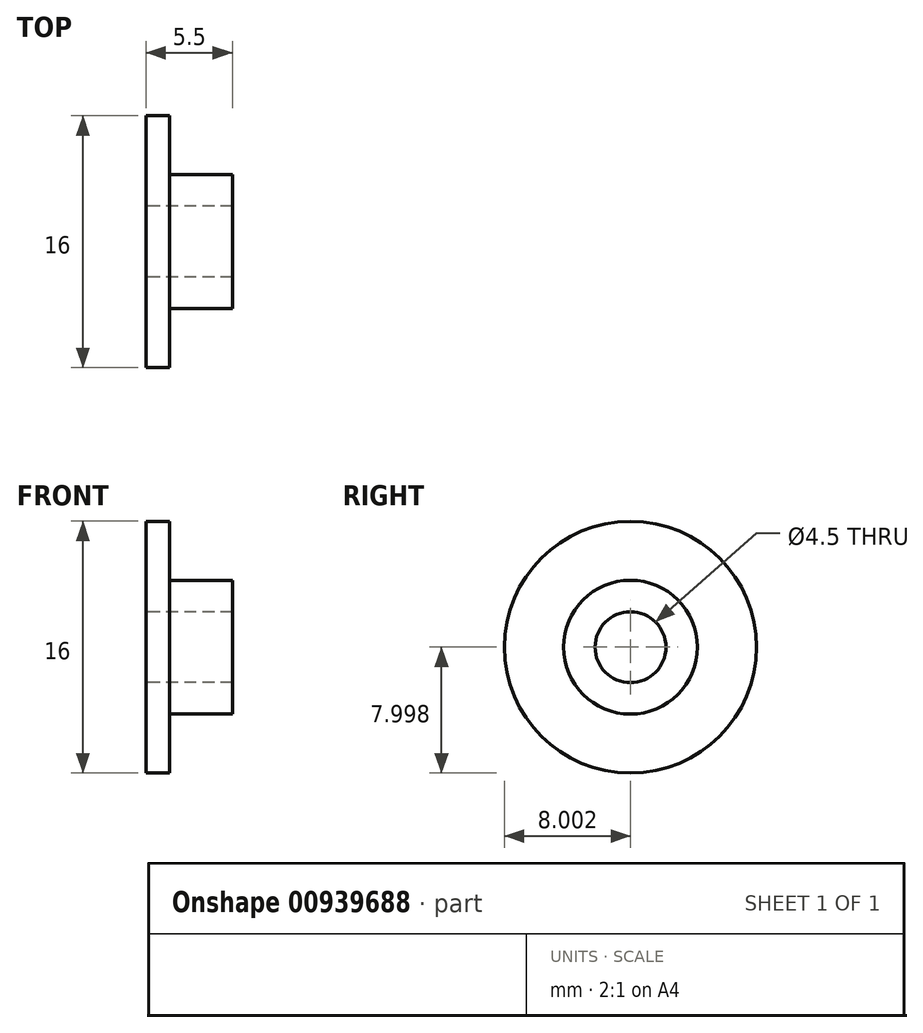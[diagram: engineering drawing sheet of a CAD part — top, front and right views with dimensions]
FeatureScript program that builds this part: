
annotation { "Feature Type Name" : "Feature", "Feature Type Description" : "" }
export const myFeature = defineFeature(function(context is Context, id is Id, definition is map)
    precondition{}
    {
        {
            var Q0;
            Q0=qCreatedBy(makeId("Right.planeOp"),FACE);
            var sketch = newSketch(context, id + "F0", { "sketchPlane" : qUnion([Q0])});
            skArc(sketch, "E0.0", {"start": v(7.2, 6.47) * mm, "mid": v(-5.3, 18.98) * mm, "end": v(-17.8, 6.47) * mm});
            skArc(sketch, "E1.0", {"start": v(9.7, 6.27) * mm, "mid": v(-5.3, 21.27) * mm, "end": v(-20.3, 6.27) * mm});
            skLineSegment(sketch, "E2.0.0", {"start": v(-20.3, -8.73) * mm, "end": v(9.7, -8.73) * mm});
            skLineSegment(sketch, "E2.0.1", {"start": v(9.7, -8.73) * mm, "end": v(9.7, -3.73) * mm});
            skLineSegment(sketch, "E2.0.2", {"start": v(9.7, -3.73) * mm, "end": v(9.7, 6.27) * mm});
            skLineSegment(sketch, "E2.0.4", {"start": v(-20.3, 6.27) * mm, "end": v(-20.3, -8.73) * mm});
            skLineSegment(sketch, "E3.0", {"start": v(-17.8, 6.47) * mm, "end": v(-17.8, -6.73) * mm});
            skLineSegment(sketch, "E4.0", {"start": v(-17.8, -6.73) * mm, "end": v(7.2, -6.73) * mm});
            skLineSegment(sketch, "E5.0", {"start": v(7.2, 6.47) * mm, "end": v(7.2, -6.73) * mm});
            skLineSegment(sketch, "E6.0.0", {"start": v(9.7, -8.73) * mm, "end": v(79.7, -8.73) * mm});
            skLineSegment(sketch, "E6.0.1", {"start": v(79.7, -8.73) * mm, "end": v(74.7, -3.73) * mm});
            skLineSegment(sketch, "E6.0.2", {"start": v(74.7, -3.73) * mm, "end": v(9.7, -3.73) * mm});
            skLineSegment(sketch, "E6.0.3", {"start": v(9.7, -3.73) * mm, "end": v(9.7, -8.73) * mm});
            skCircle(sketch, "E7", {"center": v(-5.3, 6.47) * mm, "radius": 12.5 * mm});
            skCircle(sketch, "E8", {"center": v(-5.3, 6.27) * mm, "radius": 5 * mm});
            skLineSegment(sketch, "E9", {"start": v(-17.8, 6.47) * mm, "end": v(-16.3, 6.47) * mm});
            skLineSegment(sketch, "E10", {"start": v(7.2, 6.47) * mm, "end": v(5.7, 6.47) * mm});
            skArc(sketch, "E11", {"start": v(5.7, 6.47) * mm, "mid": v(-5.3, 17.5) * mm, "end": v(-16.3, 6.47) * mm});
            skLineSegment(sketch, "E12", {"start": v(7.2, 6.47) * mm, "end": v(6.8, 6.47) * mm});
            skLineSegment(sketch, "E13", {"start": v(-17.8, 6.47) * mm, "end": v(-17.4, 6.47) * mm});
            skArc(sketch, "E14", {"start": v(6.8, 6.47) * mm, "mid": v(-5.3, 18.58) * mm, "end": v(-17.4, 6.47) * mm});
            skLineSegment(sketch, "E15", {"start": v(-17.4, 6.47) * mm, "end": v(-17.4, -6.73) * mm});
            skLineSegment(sketch, "E16", {"start": v(-16.3, 6.47) * mm, "end": v(-16.28, -6.73) * mm});
            skLineSegment(sketch, "E17", {"start": v(5.7, 6.47) * mm, "end": v(5.68, -6.73) * mm});
            skLineSegment(sketch, "E18", {"start": v(6.8, 6.47) * mm, "end": v(6.78, -6.73) * mm});
            skLineSegment(sketch, "E19", {"start": v(6.78, -6.73) * mm, "end": v(-16.28, -6.73) * mm});
            skLineSegment(sketch, "E20", {"start": v(-16.28, -6.73) * mm, "end": v(-16.28, -6.33) * mm});
            skLineSegment(sketch, "E21", {"start": v(5.68, -6.37) * mm, "end": v(5.68, -5.27) * mm});
            skLineSegment(sketch, "E22", {"start": v(5.68, -5.27) * mm, "end": v(-16.28, -5.26) * mm});
            skLineSegment(sketch, "E23", {"start": v(-16.28, -5.26) * mm, "end": v(-9.6, -5.26) * mm});
            skLineSegment(sketch, "E24", {"start": v(-1, -5.27) * mm, "end": v(5.68, -5.27) * mm});
            skLineSegment(sketch, "E25", {"start": v(5.68, -6.37) * mm, "end": v(6.78, -6.37) * mm});
            skLineSegment(sketch, "E26", {"start": v(6.78, -6.37) * mm, "end": v(-17.4, -6.36) * mm});
            skLineSegment(sketch, "E27", {"start": v(-9.6, -5.26) * mm, "end": v(-12.74, -6.36) * mm});
            skLineSegment(sketch, "E28", {"start": v(-12.74, -6.36) * mm, "end": v(-16.28, -5.26) * mm});
            skLineSegment(sketch, "E29", {"start": v(-16.28, -5.26) * mm, "end": v(-16.28, -6.33) * mm});
            skCircle(sketch, "E30", {"center": v(-5.3, 6.27) * mm, "radius": 4.25 * mm});
            skCircle(sketch, "E31", {"center": v(-5.3, 6.27) * mm, "radius": 8 * mm});
            skCircle(sketch, "E32", {"center": v(-5.3, 6.27) * mm, "radius": 2.25 * mm});
            skSolve(sketch);
        }
        {
            var Q0;
            Q0=makeQuery(id+"F0.imprint","IMPRINT",FACE,{"disambiguationData":[TD([[makeQuery(id+"F0.imprint","IMPRINT",EDGE,{"derivedFrom":sQuery(id+"F0.wireOp",EDGE,"E30")}),1.0]])]});
            extrude(context, id + "F1", {"entities" : qUnion([Q0]), "depth" : 4 * mm, "offsetDistance" : 25 * mm});
        }
        {
            var Q0;
            Q0=makeQuery(id+"F0.imprint","IMPRINT",FACE,{"disambiguationData":[TD([[makeQuery(id+"F0.imprint","IMPRINT",EDGE,{"derivedFrom":sQuery(id+"F0.wireOp",EDGE,"E30")}),1.0]])]});
            var Q1;
            Q1=makeQuery(id+"F0.imprint","IMPRINT",FACE,{"disambiguationData":[TD([[makeQuery(id+"F0.imprint","IMPRINT",EDGE,{"derivedFrom":sQuery(id+"F0.wireOp",EDGE,"E8")}),1.0]])]});
            var Q2;
            Q2=makeQuery(id+"F0.imprint","IMPRINT",FACE,{"disambiguationData":[TD([[makeQuery(id+"F0.imprint","IMPRINT",EDGE,{"derivedFrom":sQuery(id+"F0.wireOp",EDGE,"E8")}),-1.0]])]});
            extrude(context, id + "F2", {"entities" : qUnion([Q0, Q1, Q2]), "operationType" : NewBodyOperationType.ADD, "oppositeDirection" : true, "depth" : 1.5 * mm, "offsetDistance" : 25 * mm});
        }
    });
